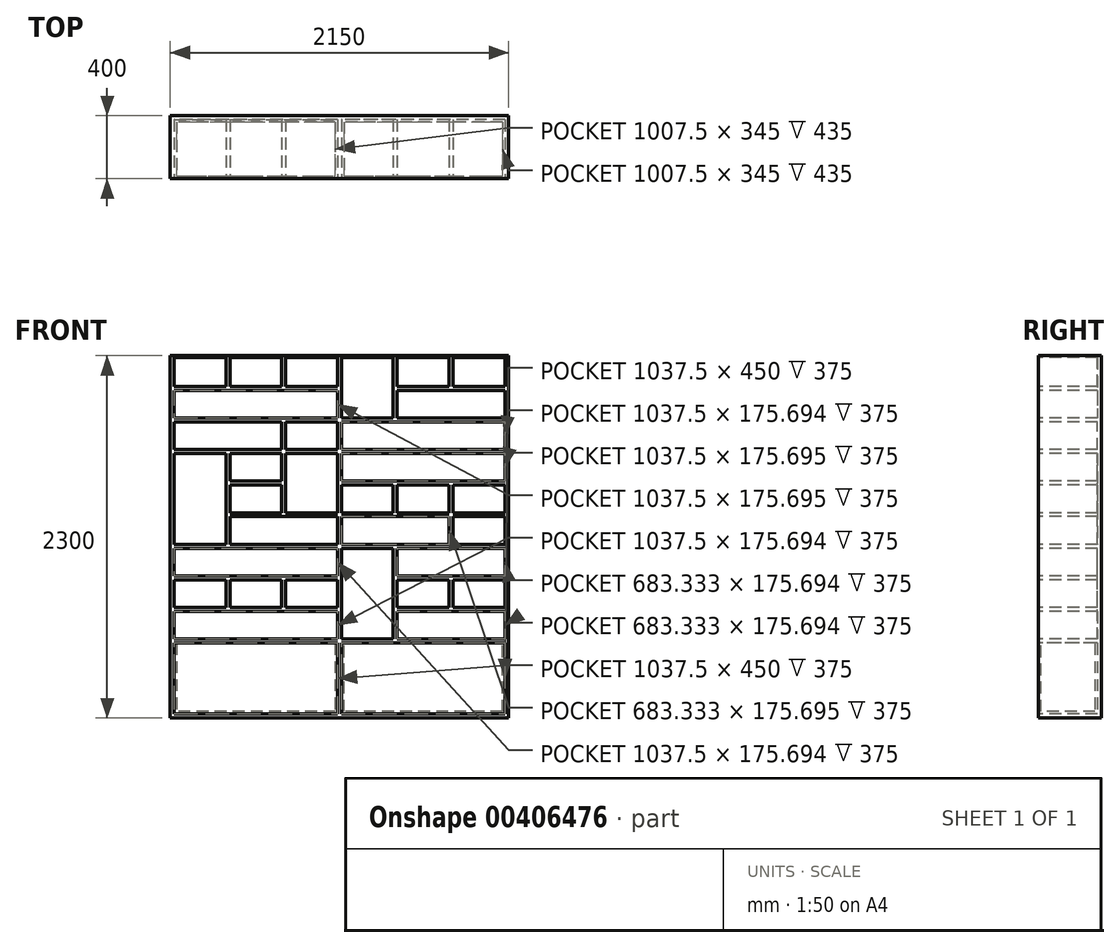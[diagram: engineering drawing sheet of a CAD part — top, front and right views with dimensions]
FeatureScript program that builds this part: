
annotation { "Feature Type Name" : "Feature", "Feature Type Description" : "" }
export const myFeature = defineFeature(function(context is Context, id is Id, definition is map)
    precondition{}
    {
        {
            var Q0;
            Q0=qCreatedBy(makeId("Front.planeOp"),FACE);
            var sketch = newSketch(context, id + "F0", { "sketchPlane" : qUnion([Q0])});
            skLineSegment(sketch, "E0.bottom", {"start": v(-1075, 0) * mm, "end": v(1075, 0) * mm});
            skLineSegment(sketch, "E0.top", {"start": v(-1075, 2300) * mm, "end": v(1075, 2300) * mm});
            skLineSegment(sketch, "E0.left", {"start": v(-1075, 0) * mm, "end": v(-1075, 2300) * mm});
            skLineSegment(sketch, "E0.right", {"start": v(1075, 0) * mm, "end": v(1075, 2300) * mm});
            skSolve(sketch);
        }
        {
            var Q0;
            Q0 = qSketchRegion(id + "F0", true);
            extrude(context, id + "F1", {"entities" : qUnion([Q0]), "depth" : 400 * mm, "offsetDistance" : 25 * mm});
        }
        {
            var Q0;
            Q0=makeQuery(id+"F1.opExtrude","CAP_FACE",FACE,{"disambiguationData":[OSD([sQuery(id+"F0.wireOp",EDGE,"E0.bottom"),sQuery(id+"F0.wireOp",EDGE,"E0.top"),sQuery(id+"F0.wireOp",EDGE,"E0.left"),sQuery(id+"F0.wireOp",EDGE,"E0.right")])],"isStart":false});
            var sketch = newSketch(context, id + "F2", { "sketchPlane" : qUnion([Q0])});
            skLineSegment(sketch, "E1", {"start": v(0, 2300) * mm, "end": v(0, 0) * mm, "construction": true});
            skLineSegment(sketch, "E2.bottom", {"start": v(-1050, 25) * mm, "end": v(-12.5, 25) * mm});
            skLineSegment(sketch, "E2.top", {"start": v(-1050, 475) * mm, "end": v(-12.5, 475) * mm});
            skLineSegment(sketch, "E2.left", {"start": v(-1050, 25) * mm, "end": v(-1050, 475) * mm});
            skLineSegment(sketch, "E2.right", {"start": v(-12.5, 25) * mm, "end": v(-12.5, 475) * mm});
            skLineSegment(sketch, "E3.bottom", {"start": v(12.5, 475) * mm, "end": v(1050, 475) * mm});
            skLineSegment(sketch, "E3.top", {"start": v(12.5, 25) * mm, "end": v(1050, 25) * mm});
            skLineSegment(sketch, "E3.left", {"start": v(12.5, 475) * mm, "end": v(12.5, 25) * mm});
            skLineSegment(sketch, "E3.right", {"start": v(1050, 475) * mm, "end": v(1050, 25) * mm});
            skLineSegment(sketch, "E4", {"start": v(-1075, 487.5) * mm, "end": v(1075, 487.5) * mm, "construction": true});
            skLineSegment(sketch, "E5", {"start": v(-1075, 1089.58) * mm, "end": v(1075, 1089.58) * mm, "construction": true});
            skLineSegment(sketch, "E6", {"start": v(-1075, 1691.67) * mm, "end": v(1075, 1691.67) * mm, "construction": true});
            skLineSegment(sketch, "E7", {"start": v(-1075, 2293.75) * mm, "end": v(1075, 2293.75) * mm, "construction": true});
            skLineSegment(sketch, "E8.bottom", {"start": v(-1050, 2287.5) * mm, "end": v(-12.5, 2287.5) * mm, "construction": true});
            skLineSegment(sketch, "E8.top", {"start": v(-1050, 1704.17) * mm, "end": v(-12.5, 1704.17) * mm, "construction": true});
            skLineSegment(sketch, "E8.left", {"start": v(-1050, 2287.5) * mm, "end": v(-1050, 1704.17) * mm, "construction": true});
            skLineSegment(sketch, "E8.right", {"start": v(-12.5, 2287.5) * mm, "end": v(-12.5, 1704.17) * mm, "construction": true});
            skLineSegment(sketch, "E9.bottom", {"start": v(-1050, 1679.17) * mm, "end": v(-12.5, 1679.17) * mm, "construction": true});
            skLineSegment(sketch, "E9.top", {"start": v(-1050, 1102.08) * mm, "end": v(-12.5, 1102.08) * mm, "construction": true});
            skLineSegment(sketch, "E9.left", {"start": v(-1050, 1679.17) * mm, "end": v(-1050, 1102.08) * mm, "construction": true});
            skLineSegment(sketch, "E9.right", {"start": v(-12.5, 1679.17) * mm, "end": v(-12.5, 1102.08) * mm, "construction": true});
            skLineSegment(sketch, "E10.bottom", {"start": v(-1050, 1077.08) * mm, "end": v(-12.5, 1077.08) * mm, "construction": true});
            skLineSegment(sketch, "E10.top", {"start": v(-1050, 500) * mm, "end": v(-12.5, 500) * mm, "construction": true});
            skLineSegment(sketch, "E10.left", {"start": v(-1050, 1077.08) * mm, "end": v(-1050, 500) * mm, "construction": true});
            skLineSegment(sketch, "E10.right", {"start": v(-12.5, 1077.08) * mm, "end": v(-12.5, 500) * mm, "construction": true});
            skLineSegment(sketch, "E11.bottom", {"start": v(12.5, 1077.08) * mm, "end": v(1050, 1077.08) * mm, "construction": true});
            skLineSegment(sketch, "E11.top", {"start": v(12.5, 500) * mm, "end": v(1050, 500) * mm, "construction": true});
            skLineSegment(sketch, "E11.left", {"start": v(12.5, 1077.08) * mm, "end": v(12.5, 500) * mm, "construction": true});
            skLineSegment(sketch, "E11.right", {"start": v(1050, 1077.08) * mm, "end": v(1050, 500) * mm, "construction": true});
            skLineSegment(sketch, "E12.bottom", {"start": v(12.5, 1679.17) * mm, "end": v(1050, 1679.17) * mm, "construction": true});
            skLineSegment(sketch, "E12.top", {"start": v(12.5, 1102.08) * mm, "end": v(1050, 1102.08) * mm, "construction": true});
            skLineSegment(sketch, "E12.left", {"start": v(12.5, 1679.17) * mm, "end": v(12.5, 1102.08) * mm, "construction": true});
            skLineSegment(sketch, "E12.right", {"start": v(1050, 1679.17) * mm, "end": v(1050, 1102.08) * mm, "construction": true});
            skLineSegment(sketch, "E13.bottom", {"start": v(12.5, 2287.5) * mm, "end": v(1050, 2287.5) * mm, "construction": true});
            skLineSegment(sketch, "E13.top", {"start": v(12.5, 1704.17) * mm, "end": v(1050, 1704.17) * mm, "construction": true});
            skLineSegment(sketch, "E13.left", {"start": v(12.5, 2287.5) * mm, "end": v(12.5, 1704.17) * mm, "construction": true});
            skLineSegment(sketch, "E13.right", {"start": v(1050, 2287.5) * mm, "end": v(1050, 1704.17) * mm, "construction": true});
            skLineSegment(sketch, "E14.bottom", {"start": v(12.5, 1704.17) * mm, "end": v(1050, 1704.17) * mm});
            skLineSegment(sketch, "E14.top", {"start": v(12.5, 1879.86) * mm, "end": v(1050, 1879.86) * mm});
            skLineSegment(sketch, "E14.left", {"start": v(12.5, 1704.17) * mm, "end": v(12.5, 1879.86) * mm});
            skLineSegment(sketch, "E14.right", {"start": v(1050, 1704.17) * mm, "end": v(1050, 1879.86) * mm});
            skLineSegment(sketch, "E15.bottom", {"start": v(12.5, 1904.86) * mm, "end": v(341.67, 1904.86) * mm});
            skLineSegment(sketch, "E15.top", {"start": v(12.5, 2287.5) * mm, "end": v(341.67, 2287.5) * mm});
            skLineSegment(sketch, "E15.left", {"start": v(12.5, 1904.86) * mm, "end": v(12.5, 2287.5) * mm});
            skLineSegment(sketch, "E15.right", {"start": v(341.67, 1904.86) * mm, "end": v(341.67, 2287.5) * mm});
            skLineSegment(sketch, "E16.bottom", {"start": v(366.67, 1904.86) * mm, "end": v(1050, 1904.86) * mm});
            skLineSegment(sketch, "E16.top", {"start": v(366.67, 2080.56) * mm, "end": v(1050, 2080.56) * mm});
            skLineSegment(sketch, "E16.left", {"start": v(366.67, 1904.86) * mm, "end": v(366.67, 2080.56) * mm});
            skLineSegment(sketch, "E16.right", {"start": v(1050, 1904.86) * mm, "end": v(1050, 2080.56) * mm});
            skLineSegment(sketch, "E17.bottom", {"start": v(366.67, 2105.56) * mm, "end": v(695.83, 2105.56) * mm});
            skLineSegment(sketch, "E17.top", {"start": v(366.67, 2287.5) * mm, "end": v(695.83, 2287.5) * mm});
            skLineSegment(sketch, "E17.left", {"start": v(366.67, 2105.56) * mm, "end": v(366.67, 2287.5) * mm});
            skLineSegment(sketch, "E17.right", {"start": v(695.83, 2105.56) * mm, "end": v(695.83, 2287.5) * mm});
            skLineSegment(sketch, "E18.bottom", {"start": v(720.83, 2287.5) * mm, "end": v(1050, 2287.5) * mm});
            skLineSegment(sketch, "E18.top", {"start": v(720.83, 2105.56) * mm, "end": v(1050, 2105.56) * mm});
            skLineSegment(sketch, "E18.left", {"start": v(720.83, 2287.5) * mm, "end": v(720.83, 2105.56) * mm});
            skLineSegment(sketch, "E18.right", {"start": v(1050, 2287.5) * mm, "end": v(1050, 2105.56) * mm});
            skLineSegment(sketch, "E19", {"start": v(354.17, 2293.75) * mm, "end": v(354.17, 1691.67) * mm, "construction": true});
            skLineSegment(sketch, "E20", {"start": v(708.33, 2293.75) * mm, "end": v(708.33, 1691.67) * mm, "construction": true});
            skLineSegment(sketch, "E21", {"start": v(1062.5, 2293.75) * mm, "end": v(1062.5, 1691.67) * mm, "construction": true});
            skLineSegment(sketch, "E22", {"start": v(0, 1892.36) * mm, "end": v(1062.5, 1892.36) * mm, "construction": true});
            skLineSegment(sketch, "E23", {"start": v(1062.5, 2093.06) * mm, "end": v(0, 2093.06) * mm, "construction": true});
            skLineSegment(sketch, "E24.bottom", {"start": v(-12.5, 1904.86) * mm, "end": v(-1050, 1904.86) * mm});
            skLineSegment(sketch, "E24.top", {"start": v(-12.5, 2080.56) * mm, "end": v(-1050, 2080.56) * mm});
            skLineSegment(sketch, "E24.left", {"start": v(-12.5, 1904.86) * mm, "end": v(-12.5, 2080.56) * mm});
            skLineSegment(sketch, "E24.right", {"start": v(-1050, 1904.86) * mm, "end": v(-1050, 2080.56) * mm});
            skLineSegment(sketch, "E25.bottom", {"start": v(-12.5, 1879.86) * mm, "end": v(-341.67, 1879.86) * mm});
            skLineSegment(sketch, "E25.top", {"start": v(-12.5, 1704.17) * mm, "end": v(-341.67, 1704.17) * mm});
            skLineSegment(sketch, "E25.left", {"start": v(-12.5, 1879.86) * mm, "end": v(-12.5, 1704.17) * mm});
            skLineSegment(sketch, "E25.right", {"start": v(-341.67, 1879.86) * mm, "end": v(-341.67, 1704.17) * mm});
            skLineSegment(sketch, "E26.bottom", {"start": v(-1050, 1879.86) * mm, "end": v(-366.67, 1879.86) * mm});
            skLineSegment(sketch, "E26.top", {"start": v(-1050, 1704.17) * mm, "end": v(-366.67, 1704.17) * mm});
            skLineSegment(sketch, "E26.left", {"start": v(-1050, 1879.86) * mm, "end": v(-1050, 1704.17) * mm});
            skLineSegment(sketch, "E26.right", {"start": v(-366.67, 1879.86) * mm, "end": v(-366.67, 1704.17) * mm});
            skLineSegment(sketch, "E27.bottom", {"start": v(-12.5, 2287.5) * mm, "end": v(-341.67, 2287.5) * mm});
            skLineSegment(sketch, "E27.top", {"start": v(-12.5, 2105.56) * mm, "end": v(-341.67, 2105.56) * mm});
            skLineSegment(sketch, "E27.left", {"start": v(-12.5, 2287.5) * mm, "end": v(-12.5, 2105.56) * mm});
            skLineSegment(sketch, "E27.right", {"start": v(-341.67, 2287.5) * mm, "end": v(-341.67, 2105.56) * mm});
            skLineSegment(sketch, "E28.bottom", {"start": v(-366.67, 2105.56) * mm, "end": v(-695.83, 2105.56) * mm});
            skLineSegment(sketch, "E28.top", {"start": v(-366.67, 2287.5) * mm, "end": v(-695.83, 2287.5) * mm});
            skLineSegment(sketch, "E28.left", {"start": v(-366.67, 2105.56) * mm, "end": v(-366.67, 2287.5) * mm});
            skLineSegment(sketch, "E28.right", {"start": v(-695.83, 2105.56) * mm, "end": v(-695.83, 2287.5) * mm});
            skLineSegment(sketch, "E29.bottom", {"start": v(-720.83, 2287.5) * mm, "end": v(-1050, 2287.5) * mm});
            skLineSegment(sketch, "E29.top", {"start": v(-720.83, 2105.56) * mm, "end": v(-1050, 2105.56) * mm});
            skLineSegment(sketch, "E29.left", {"start": v(-720.83, 2287.5) * mm, "end": v(-720.83, 2105.56) * mm});
            skLineSegment(sketch, "E29.right", {"start": v(-1050, 2287.5) * mm, "end": v(-1050, 2105.56) * mm});
            skLineSegment(sketch, "E30.bottom", {"start": v(12.5, 1679.17) * mm, "end": v(1050, 1679.17) * mm});
            skLineSegment(sketch, "E30.top", {"start": v(12.5, 1503.47) * mm, "end": v(1050, 1503.47) * mm});
            skLineSegment(sketch, "E30.left", {"start": v(12.5, 1679.17) * mm, "end": v(12.5, 1503.47) * mm});
            skLineSegment(sketch, "E30.right", {"start": v(1050, 1679.17) * mm, "end": v(1050, 1503.47) * mm});
            skLineSegment(sketch, "E31.bottom", {"start": v(12.5, 1478.47) * mm, "end": v(341.67, 1478.47) * mm});
            skLineSegment(sketch, "E31.top", {"start": v(12.5, 1302.78) * mm, "end": v(341.67, 1302.78) * mm});
            skLineSegment(sketch, "E31.left", {"start": v(12.5, 1478.47) * mm, "end": v(12.5, 1302.78) * mm});
            skLineSegment(sketch, "E31.right", {"start": v(341.67, 1478.47) * mm, "end": v(341.67, 1302.78) * mm});
            skLineSegment(sketch, "E32.bottom", {"start": v(366.67, 1478.47) * mm, "end": v(695.83, 1478.47) * mm});
            skLineSegment(sketch, "E32.top", {"start": v(366.67, 1302.78) * mm, "end": v(695.83, 1302.78) * mm});
            skLineSegment(sketch, "E32.left", {"start": v(366.67, 1478.47) * mm, "end": v(366.67, 1302.78) * mm});
            skLineSegment(sketch, "E32.right", {"start": v(695.83, 1478.47) * mm, "end": v(695.83, 1302.78) * mm});
            skLineSegment(sketch, "E33.bottom", {"start": v(720.83, 1478.47) * mm, "end": v(1050, 1478.47) * mm});
            skLineSegment(sketch, "E33.top", {"start": v(720.83, 1302.78) * mm, "end": v(1050, 1302.78) * mm});
            skLineSegment(sketch, "E33.left", {"start": v(720.83, 1478.47) * mm, "end": v(720.83, 1302.78) * mm});
            skLineSegment(sketch, "E33.right", {"start": v(1050, 1478.47) * mm, "end": v(1050, 1302.78) * mm});
            skLineSegment(sketch, "E34.bottom", {"start": v(12.5, 1277.78) * mm, "end": v(695.83, 1277.78) * mm});
            skLineSegment(sketch, "E34.top", {"start": v(12.5, 1102.08) * mm, "end": v(695.83, 1102.08) * mm});
            skLineSegment(sketch, "E34.left", {"start": v(12.5, 1277.78) * mm, "end": v(12.5, 1102.08) * mm});
            skLineSegment(sketch, "E34.right", {"start": v(695.83, 1277.78) * mm, "end": v(695.83, 1102.08) * mm});
            skLineSegment(sketch, "E35.bottom", {"start": v(720.83, 1277.78) * mm, "end": v(1050, 1277.78) * mm});
            skLineSegment(sketch, "E35.top", {"start": v(720.83, 1102.08) * mm, "end": v(1050, 1102.08) * mm});
            skLineSegment(sketch, "E35.left", {"start": v(720.83, 1277.78) * mm, "end": v(720.83, 1102.08) * mm});
            skLineSegment(sketch, "E35.right", {"start": v(1050, 1277.78) * mm, "end": v(1050, 1102.08) * mm});
            skLineSegment(sketch, "E36.bottom", {"start": v(-1050, 1102.08) * mm, "end": v(-720.83, 1102.08) * mm});
            skLineSegment(sketch, "E36.top", {"start": v(-1050, 1679.17) * mm, "end": v(-720.83, 1679.17) * mm});
            skLineSegment(sketch, "E36.left", {"start": v(-1050, 1102.08) * mm, "end": v(-1050, 1679.17) * mm});
            skLineSegment(sketch, "E36.right", {"start": v(-720.83, 1102.08) * mm, "end": v(-720.83, 1679.17) * mm});
            skLineSegment(sketch, "E37.bottom", {"start": v(-12.5, 1277.78) * mm, "end": v(-695.83, 1277.78) * mm});
            skLineSegment(sketch, "E37.top", {"start": v(-12.5, 1102.08) * mm, "end": v(-695.83, 1102.08) * mm});
            skLineSegment(sketch, "E37.left", {"start": v(-12.5, 1277.78) * mm, "end": v(-12.5, 1102.08) * mm});
            skLineSegment(sketch, "E37.right", {"start": v(-695.83, 1277.78) * mm, "end": v(-695.83, 1102.08) * mm});
            skLineSegment(sketch, "E38.bottom", {"start": v(-12.5, 1679.17) * mm, "end": v(-341.67, 1679.17) * mm});
            skLineSegment(sketch, "E38.top", {"start": v(-12.5, 1302.78) * mm, "end": v(-341.67, 1302.78) * mm});
            skLineSegment(sketch, "E38.left", {"start": v(-12.5, 1679.17) * mm, "end": v(-12.5, 1302.78) * mm});
            skLineSegment(sketch, "E38.right", {"start": v(-341.67, 1679.17) * mm, "end": v(-341.67, 1302.78) * mm});
            skLineSegment(sketch, "E39.bottom", {"start": v(-695.83, 1302.78) * mm, "end": v(-366.67, 1302.78) * mm});
            skLineSegment(sketch, "E39.top", {"start": v(-695.83, 1478.47) * mm, "end": v(-366.67, 1478.47) * mm});
            skLineSegment(sketch, "E39.left", {"start": v(-695.83, 1302.78) * mm, "end": v(-695.83, 1478.47) * mm});
            skLineSegment(sketch, "E39.right", {"start": v(-366.67, 1302.78) * mm, "end": v(-366.67, 1478.47) * mm});
            skLineSegment(sketch, "E40.bottom", {"start": v(-695.83, 1679.17) * mm, "end": v(-366.67, 1679.17) * mm});
            skLineSegment(sketch, "E40.top", {"start": v(-695.83, 1503.47) * mm, "end": v(-366.67, 1503.47) * mm});
            skLineSegment(sketch, "E40.left", {"start": v(-695.83, 1679.17) * mm, "end": v(-695.83, 1503.47) * mm});
            skLineSegment(sketch, "E40.right", {"start": v(-366.67, 1679.17) * mm, "end": v(-366.67, 1503.47) * mm});
            skLineSegment(sketch, "E41.bottom", {"start": v(-1050, 1077.08) * mm, "end": v(-12.5, 1077.08) * mm});
            skLineSegment(sketch, "E41.top", {"start": v(-1050, 901.39) * mm, "end": v(-12.5, 901.39) * mm});
            skLineSegment(sketch, "E41.left", {"start": v(-1050, 1077.08) * mm, "end": v(-1050, 901.39) * mm});
            skLineSegment(sketch, "E41.right", {"start": v(-12.5, 1077.08) * mm, "end": v(-12.5, 901.39) * mm});
            skLineSegment(sketch, "E42.bottom", {"start": v(-12.5, 500) * mm, "end": v(-1050, 500) * mm});
            skLineSegment(sketch, "E42.top", {"start": v(-12.5, 675.7) * mm, "end": v(-1050, 675.7) * mm});
            skLineSegment(sketch, "E42.left", {"start": v(-12.5, 500) * mm, "end": v(-12.5, 675.7) * mm});
            skLineSegment(sketch, "E42.right", {"start": v(-1050, 500) * mm, "end": v(-1050, 675.7) * mm});
            skLineSegment(sketch, "E43.bottom", {"start": v(-1050, 876.39) * mm, "end": v(-720.83, 876.39) * mm});
            skLineSegment(sketch, "E43.top", {"start": v(-1050, 700.7) * mm, "end": v(-720.83, 700.7) * mm});
            skLineSegment(sketch, "E43.left", {"start": v(-1050, 876.39) * mm, "end": v(-1050, 700.7) * mm});
            skLineSegment(sketch, "E43.right", {"start": v(-720.83, 876.39) * mm, "end": v(-720.83, 700.7) * mm});
            skLineSegment(sketch, "E44.bottom", {"start": v(-341.67, 876.39) * mm, "end": v(-12.5, 876.39) * mm});
            skLineSegment(sketch, "E44.top", {"start": v(-341.67, 700.7) * mm, "end": v(-12.5, 700.7) * mm});
            skLineSegment(sketch, "E44.left", {"start": v(-341.67, 876.39) * mm, "end": v(-341.67, 700.7) * mm});
            skLineSegment(sketch, "E44.right", {"start": v(-12.5, 876.39) * mm, "end": v(-12.5, 700.7) * mm});
            skLineSegment(sketch, "E45.bottom", {"start": v(-695.83, 876.39) * mm, "end": v(-366.67, 876.39) * mm});
            skLineSegment(sketch, "E45.top", {"start": v(-695.83, 700.7) * mm, "end": v(-366.67, 700.7) * mm});
            skLineSegment(sketch, "E45.left", {"start": v(-695.83, 876.39) * mm, "end": v(-695.83, 700.7) * mm});
            skLineSegment(sketch, "E45.right", {"start": v(-366.67, 876.39) * mm, "end": v(-366.67, 700.7) * mm});
            skLineSegment(sketch, "E46.bottom", {"start": v(12.5, 1077.08) * mm, "end": v(341.67, 1077.08) * mm});
            skLineSegment(sketch, "E46.top", {"start": v(12.5, 500) * mm, "end": v(341.67, 500) * mm});
            skLineSegment(sketch, "E46.left", {"start": v(12.5, 1077.08) * mm, "end": v(12.5, 500) * mm});
            skLineSegment(sketch, "E46.right", {"start": v(341.67, 1077.08) * mm, "end": v(341.67, 500) * mm});
            skLineSegment(sketch, "E47.bottom", {"start": v(366.67, 1077.08) * mm, "end": v(1050, 1077.08) * mm});
            skLineSegment(sketch, "E47.top", {"start": v(366.67, 901.39) * mm, "end": v(1050, 901.39) * mm});
            skLineSegment(sketch, "E47.left", {"start": v(366.67, 1077.08) * mm, "end": v(366.67, 901.39) * mm});
            skLineSegment(sketch, "E47.right", {"start": v(1050, 1077.08) * mm, "end": v(1050, 901.39) * mm});
            skLineSegment(sketch, "E48.bottom", {"start": v(366.67, 500) * mm, "end": v(1050, 500) * mm});
            skLineSegment(sketch, "E48.top", {"start": v(366.67, 675.7) * mm, "end": v(1050, 675.7) * mm});
            skLineSegment(sketch, "E48.left", {"start": v(366.67, 500) * mm, "end": v(366.67, 675.7) * mm});
            skLineSegment(sketch, "E48.right", {"start": v(1050, 500) * mm, "end": v(1050, 675.7) * mm});
            skLineSegment(sketch, "E49.bottom", {"start": v(366.67, 876.39) * mm, "end": v(695.83, 876.39) * mm});
            skLineSegment(sketch, "E49.top", {"start": v(366.67, 700.7) * mm, "end": v(695.83, 700.7) * mm});
            skLineSegment(sketch, "E49.left", {"start": v(366.67, 876.39) * mm, "end": v(366.67, 700.7) * mm});
            skLineSegment(sketch, "E49.right", {"start": v(695.83, 876.39) * mm, "end": v(695.83, 700.7) * mm});
            skLineSegment(sketch, "E50.bottom", {"start": v(720.83, 876.39) * mm, "end": v(1050, 876.39) * mm});
            skLineSegment(sketch, "E50.top", {"start": v(720.83, 700.7) * mm, "end": v(1050, 700.7) * mm});
            skLineSegment(sketch, "E50.left", {"start": v(720.83, 876.39) * mm, "end": v(720.83, 700.7) * mm});
            skLineSegment(sketch, "E50.right", {"start": v(1050, 876.39) * mm, "end": v(1050, 700.7) * mm});
            skSolve(sketch);
        }
        {
            var Q0;
            Q0=makeQuery(id+"F2.imprint","IMPRINT",FACE,{"disambiguationData":[TD([[makeQuery(id+"F2.imprint","IMPRINT",EDGE,{"derivedFrom":sQuery(id+"F2.wireOp",EDGE,"E29.bottom")}),1.0]])]});
            var Q1;
            Q1=makeQuery(id+"F2.imprint","IMPRINT",FACE,{"disambiguationData":[TD([[makeQuery(id+"F2.imprint","IMPRINT",EDGE,{"derivedFrom":sQuery(id+"F2.wireOp",EDGE,"E28.bottom")}),-1.0]])]});
            var Q2;
            Q2=makeQuery(id+"F2.imprint","IMPRINT",FACE,{"disambiguationData":[TD([[makeQuery(id+"F2.imprint","IMPRINT",EDGE,{"derivedFrom":sQuery(id+"F2.wireOp",EDGE,"E27.bottom")}),1.0]])]});
            var Q3;
            Q3=makeQuery(id+"F2.imprint","IMPRINT",FACE,{"disambiguationData":[TD([[makeQuery(id+"F2.imprint","IMPRINT",EDGE,{"derivedFrom":sQuery(id+"F2.wireOp",EDGE,"E15.bottom")}),1.0]])]});
            var Q4;
            Q4=makeQuery(id+"F2.imprint","IMPRINT",FACE,{"disambiguationData":[TD([[makeQuery(id+"F2.imprint","IMPRINT",EDGE,{"derivedFrom":sQuery(id+"F2.wireOp",EDGE,"E17.bottom")}),1.0]])]});
            var Q5;
            Q5=makeQuery(id+"F2.imprint","IMPRINT",FACE,{"disambiguationData":[TD([[makeQuery(id+"F2.imprint","IMPRINT",EDGE,{"derivedFrom":sQuery(id+"F2.wireOp",EDGE,"E18.bottom")}),-1.0]])]});
            var Q6;
            Q6=makeQuery(id+"F2.imprint","IMPRINT",FACE,{"disambiguationData":[TD([[makeQuery(id+"F2.imprint","IMPRINT",EDGE,{"derivedFrom":sQuery(id+"F2.wireOp",EDGE,"E24.bottom")}),-1.0]])]});
            var Q7;
            Q7=makeQuery(id+"F2.imprint","IMPRINT",FACE,{"disambiguationData":[TD([[makeQuery(id+"F2.imprint","IMPRINT",EDGE,{"derivedFrom":sQuery(id+"F2.wireOp",EDGE,"E16.bottom")}),1.0]])]});
            var Q8;
            Q8=makeQuery(id+"F2.imprint","IMPRINT",FACE,{"disambiguationData":[TD([[makeQuery(id+"F2.imprint","IMPRINT",EDGE,{"derivedFrom":sQuery(id+"F2.wireOp",EDGE,"E26.bottom")}),-1.0]])]});
            var Q9;
            Q9=makeQuery(id+"F2.imprint","IMPRINT",FACE,{"disambiguationData":[TD([[makeQuery(id+"F2.imprint","IMPRINT",EDGE,{"derivedFrom":sQuery(id+"F2.wireOp",EDGE,"E25.bottom")}),1.0]])]});
            var Q10;
            Q10=makeQuery(id+"F2.imprint","IMPRINT",FACE,{"disambiguationData":[TD([[makeQuery(id+"F2.imprint","IMPRINT",EDGE,{"derivedFrom":sQuery(id+"F2.wireOp",EDGE,"E14.bottom")}),1.0]])]});
            var Q11;
            Q11=makeQuery(id+"F2.imprint","IMPRINT",FACE,{"disambiguationData":[TD([[makeQuery(id+"F2.imprint","IMPRINT",EDGE,{"derivedFrom":sQuery(id+"F2.wireOp",EDGE,"E36.bottom")}),1.0]])]});
            var Q12;
            Q12=makeQuery(id+"F2.imprint","IMPRINT",FACE,{"disambiguationData":[TD([[makeQuery(id+"F2.imprint","IMPRINT",EDGE,{"derivedFrom":sQuery(id+"F2.wireOp",EDGE,"E40.bottom")}),-1.0]])]});
            var Q13;
            Q13=makeQuery(id+"F2.imprint","IMPRINT",FACE,{"disambiguationData":[TD([[makeQuery(id+"F2.imprint","IMPRINT",EDGE,{"derivedFrom":sQuery(id+"F2.wireOp",EDGE,"E39.bottom")}),1.0]])]});
            var Q14;
            Q14=makeQuery(id+"F2.imprint","IMPRINT",FACE,{"disambiguationData":[TD([[makeQuery(id+"F2.imprint","IMPRINT",EDGE,{"derivedFrom":sQuery(id+"F2.wireOp",EDGE,"E37.bottom")}),1.0]])]});
            var Q15;
            Q15=makeQuery(id+"F2.imprint","IMPRINT",FACE,{"disambiguationData":[TD([[makeQuery(id+"F2.imprint","IMPRINT",EDGE,{"derivedFrom":sQuery(id+"F2.wireOp",EDGE,"E38.bottom")}),1.0]])]});
            var Q16;
            Q16=makeQuery(id+"F2.imprint","IMPRINT",FACE,{"disambiguationData":[TD([[makeQuery(id+"F2.imprint","IMPRINT",EDGE,{"derivedFrom":sQuery(id+"F2.wireOp",EDGE,"E30.bottom")}),-1.0]])]});
            var Q17;
            Q17=makeQuery(id+"F2.imprint","IMPRINT",FACE,{"disambiguationData":[TD([[makeQuery(id+"F2.imprint","IMPRINT",EDGE,{"derivedFrom":sQuery(id+"F2.wireOp",EDGE,"E31.bottom")}),-1.0]])]});
            var Q18;
            Q18=makeQuery(id+"F2.imprint","IMPRINT",FACE,{"disambiguationData":[TD([[makeQuery(id+"F2.imprint","IMPRINT",EDGE,{"derivedFrom":sQuery(id+"F2.wireOp",EDGE,"E32.bottom")}),-1.0]])]});
            var Q19;
            Q19=makeQuery(id+"F2.imprint","IMPRINT",FACE,{"disambiguationData":[TD([[makeQuery(id+"F2.imprint","IMPRINT",EDGE,{"derivedFrom":sQuery(id+"F2.wireOp",EDGE,"E33.bottom")}),-1.0]])]});
            var Q20;
            Q20=makeQuery(id+"F2.imprint","IMPRINT",FACE,{"disambiguationData":[TD([[makeQuery(id+"F2.imprint","IMPRINT",EDGE,{"derivedFrom":sQuery(id+"F2.wireOp",EDGE,"E34.bottom")}),-1.0]])]});
            var Q21;
            Q21=makeQuery(id+"F2.imprint","IMPRINT",FACE,{"disambiguationData":[TD([[makeQuery(id+"F2.imprint","IMPRINT",EDGE,{"derivedFrom":sQuery(id+"F2.wireOp",EDGE,"E35.bottom")}),-1.0]])]});
            var Q22;
            Q22=makeQuery(id+"F2.imprint","IMPRINT",FACE,{"disambiguationData":[TD([[makeQuery(id+"F2.imprint","IMPRINT",EDGE,{"derivedFrom":sQuery(id+"F2.wireOp",EDGE,"E41.bottom")}),-1.0]])]});
            var Q23;
            Q23=makeQuery(id+"F2.imprint","IMPRINT",FACE,{"disambiguationData":[TD([[makeQuery(id+"F2.imprint","IMPRINT",EDGE,{"derivedFrom":sQuery(id+"F2.wireOp",EDGE,"E43.bottom")}),-1.0]])]});
            var Q24;
            Q24=makeQuery(id+"F2.imprint","IMPRINT",FACE,{"disambiguationData":[TD([[makeQuery(id+"F2.imprint","IMPRINT",EDGE,{"derivedFrom":sQuery(id+"F2.wireOp",EDGE,"E45.bottom")}),-1.0]])]});
            var Q25;
            Q25=makeQuery(id+"F2.imprint","IMPRINT",FACE,{"disambiguationData":[TD([[makeQuery(id+"F2.imprint","IMPRINT",EDGE,{"derivedFrom":sQuery(id+"F2.wireOp",EDGE,"E44.bottom")}),-1.0]])]});
            var Q26;
            Q26=makeQuery(id+"F2.imprint","IMPRINT",FACE,{"disambiguationData":[TD([[makeQuery(id+"F2.imprint","IMPRINT",EDGE,{"derivedFrom":sQuery(id+"F2.wireOp",EDGE,"E42.bottom")}),-1.0]])]});
            var Q27;
            Q27=makeQuery(id+"F2.imprint","IMPRINT",FACE,{"disambiguationData":[TD([[makeQuery(id+"F2.imprint","IMPRINT",EDGE,{"derivedFrom":sQuery(id+"F2.wireOp",EDGE,"E46.bottom")}),-1.0]])]});
            var Q28;
            Q28=makeQuery(id+"F2.imprint","IMPRINT",FACE,{"disambiguationData":[TD([[makeQuery(id+"F2.imprint","IMPRINT",EDGE,{"derivedFrom":sQuery(id+"F2.wireOp",EDGE,"E47.bottom")}),-1.0]])]});
            var Q29;
            Q29=makeQuery(id+"F2.imprint","IMPRINT",FACE,{"disambiguationData":[TD([[makeQuery(id+"F2.imprint","IMPRINT",EDGE,{"derivedFrom":sQuery(id+"F2.wireOp",EDGE,"E49.bottom")}),-1.0]])]});
            var Q30;
            Q30=makeQuery(id+"F2.imprint","IMPRINT",FACE,{"disambiguationData":[TD([[makeQuery(id+"F2.imprint","IMPRINT",EDGE,{"derivedFrom":sQuery(id+"F2.wireOp",EDGE,"E50.bottom")}),-1.0]])]});
            var Q31;
            Q31=makeQuery(id+"F2.imprint","IMPRINT",FACE,{"disambiguationData":[TD([[makeQuery(id+"F2.imprint","IMPRINT",EDGE,{"derivedFrom":sQuery(id+"F2.wireOp",EDGE,"E48.bottom")}),1.0]])]});
            var Q32;
            Q32=makeQuery(id+"F2.imprint","IMPRINT",FACE,{"disambiguationData":[TD([[makeQuery(id+"F2.imprint","IMPRINT",EDGE,{"derivedFrom":sQuery(id+"F2.wireOp",EDGE,"E2.bottom")}),1.0]])]});
            var Q33;
            Q33=makeQuery(id+"F2.imprint","IMPRINT",FACE,{"disambiguationData":[TD([[makeQuery(id+"F2.imprint","IMPRINT",EDGE,{"derivedFrom":sQuery(id+"F2.wireOp",EDGE,"E3.bottom")}),-1.0]])]});
            extrude(context, id + "F3", {"entities" : qUnion([Q0, Q1, Q2, Q3, Q4, Q5, Q6, Q7, Q8, Q9, Q10, Q11, Q12, Q13, Q14, Q15, Q16, Q17, Q18, Q19, Q20, Q21, Q22, Q23, Q24, Q25, Q26, Q27, Q28, Q29, Q30, Q31, Q32, Q33]), "operationType" : NewBodyOperationType.REMOVE, "endBound" : BoundingType.UP_TO_NEXT, "oppositeDirection" : true, "depth" : 25 * mm, "hasOffset" : true, "offsetDistance" : 25 * mm});
        }
        {
            var Q0;
            Q0=makeQuery(id+"F2.imprint","IMPRINT",FACE,{"disambiguationData":[TD([[makeQuery(id+"F2.imprint","IMPRINT",EDGE,{"derivedFrom":sQuery(id+"F2.wireOp",EDGE,"E2.bottom")}),1.0]])]});
            var Q1;
            Q1=makeQuery(id+"F2.imprint","IMPRINT",FACE,{"disambiguationData":[TD([[makeQuery(id+"F2.imprint","IMPRINT",EDGE,{"derivedFrom":sQuery(id+"F2.wireOp",EDGE,"E3.bottom")}),-1.0]])]});
            extrude(context, id + "F4", {"entities" : qUnion([Q0, Q1]), "endBound" : BoundingType.UP_TO_NEXT, "oppositeDirection" : true, "depth" : 25 * mm, "offsetDistance" : 25 * mm});
        }
        {
            var Q0;
            Q0=makeQuery(id+"F4.opExtrude","SWEPT_FACE",FACE,{"disambiguationData":[OSD([sQuery(id+"F2.wireOp",EDGE,"E2.top")])]});
            var Q1;
            Q1=makeQuery(id+"F4.opExtrude","SWEPT_FACE",FACE,{"disambiguationData":[OSD([sQuery(id+"F2.wireOp",EDGE,"E3.bottom")])]});
            shell(context, id + "F5", {"entities" : qUnion([Q0, Q1]), "thickness" : 15 * mm});
        }
    });
